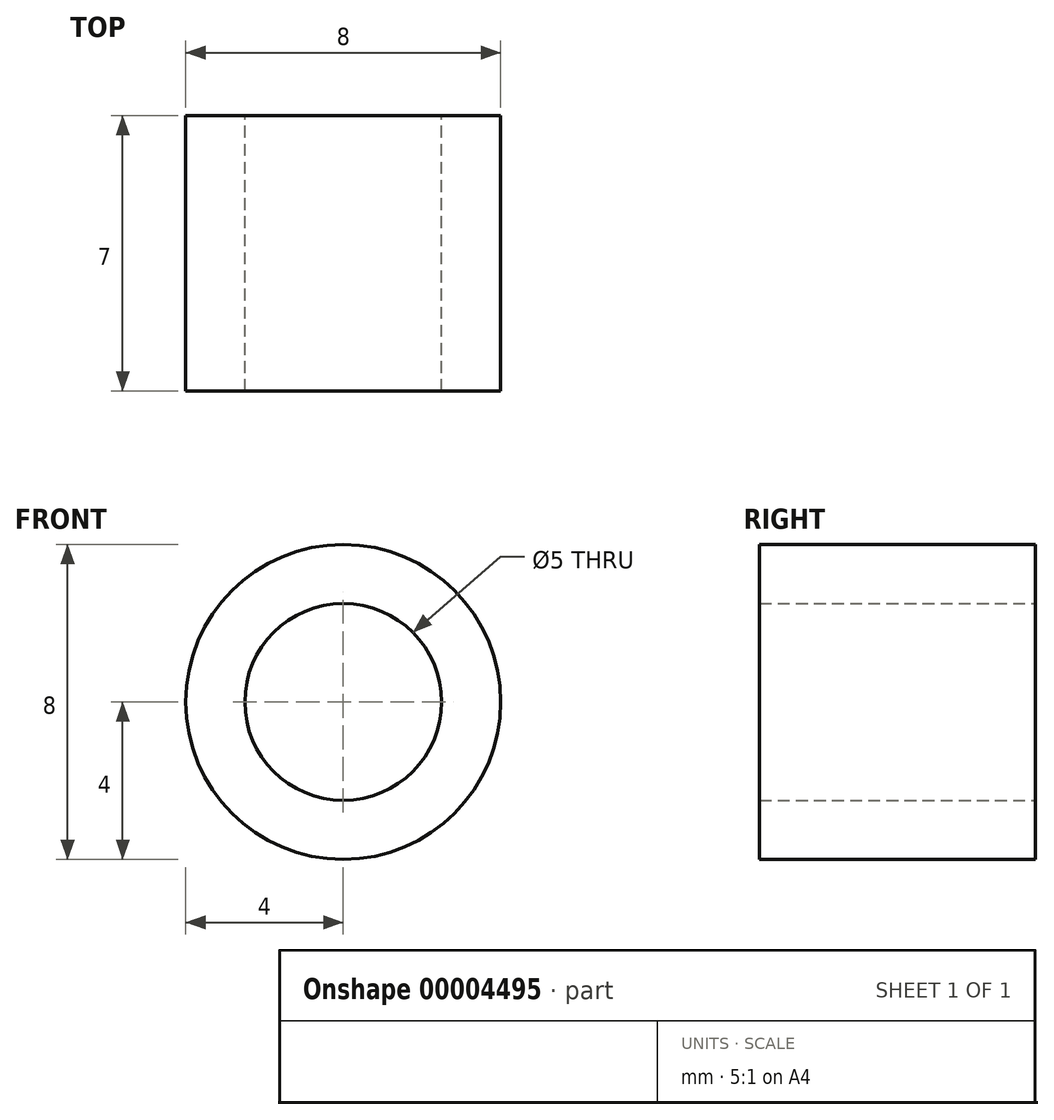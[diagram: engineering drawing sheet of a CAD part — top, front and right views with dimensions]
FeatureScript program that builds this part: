
annotation { "Feature Type Name" : "Feature", "Feature Type Description" : "" }
export const myFeature = defineFeature(function(context is Context, id is Id, definition is map)
    precondition{}
    {
        {
            var Q0;
            Q0=qCreatedBy(makeId("Front.planeOp"),FACE);
            var sketch = newSketch(context, id + "F0", { "sketchPlane" : qUnion([Q0])});
            skCircle(sketch, "E0", {"center": v(0, 0) * mm, "radius": 4 * mm});
            skCircle(sketch, "E1", {"center": v(0, 0) * mm, "radius": 2.5 * mm});
            skSolve(sketch);
        }
        {
            var Q0;
            Q0=makeQuery(id+"F0.imprint","IMPRINT",FACE,{"disambiguationData":[TD([[makeQuery(id+"F0.imprint","IMPRINT",EDGE,{"derivedFrom":sQuery(id+"F0.wireOp",EDGE,"E0")}),1.0]])]});
            extrude(context, id + "F1", {"entities" : qUnion([Q0]), "depth" : 7 * mm});
        }
    });
